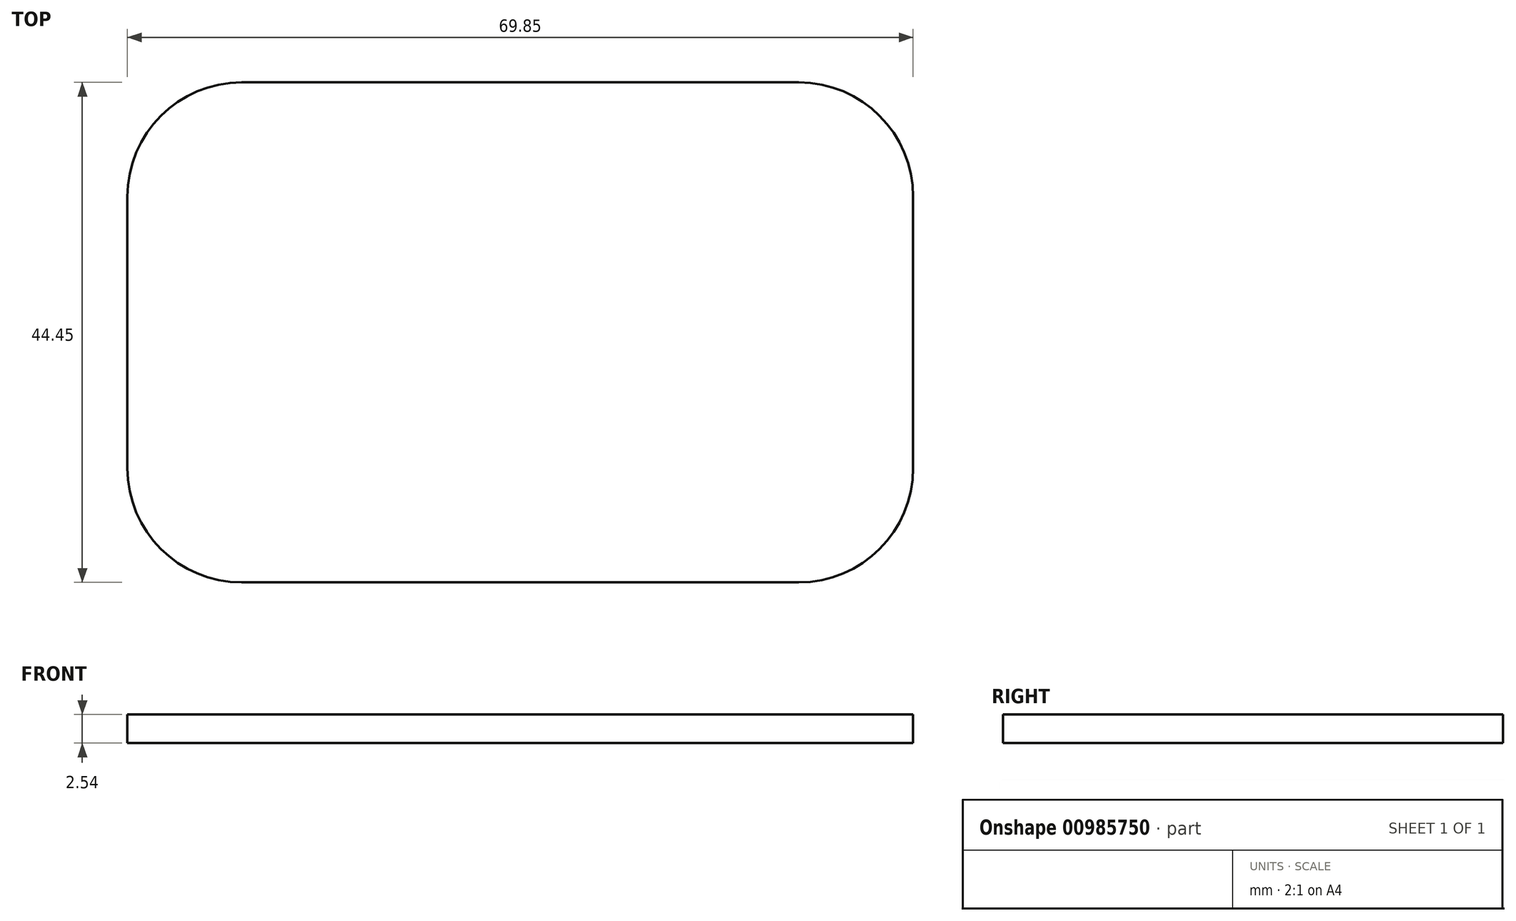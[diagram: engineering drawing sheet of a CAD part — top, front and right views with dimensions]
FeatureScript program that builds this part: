
annotation { "Feature Type Name" : "Feature", "Feature Type Description" : "" }
export const myFeature = defineFeature(function(context is Context, id is Id, definition is map)
    precondition{}
    {
        {
            var Q0;
            Q0=qCreatedBy(makeId("Top.planeOp"),FACE);
            var sketch = newSketch(context, id + "F0", { "sketchPlane" : qUnion([Q0])});
            skLineSegment(sketch, "E0.bottom", {"start": v(10.16, 0) * mm, "end": v(59.7, 0) * mm});
            skLineSegment(sketch, "E0.top", {"start": v(10.16, 44.45) * mm, "end": v(59.7, 44.45) * mm});
            skLineSegment(sketch, "E0.left", {"start": v(0, 10.16) * mm, "end": v(0, 34.3) * mm});
            skLineSegment(sketch, "E0.right", {"start": v(69.85, 10.16) * mm, "end": v(69.85, 34.3) * mm});
            skPoint(sketch, "E1.visualSharp", {"position": v(0, 44.45) * mm});
            skArc(sketch, "E1.filletArc", {"start": v(10.16, 44.45) * mm, "mid": v(2.98, 41.47) * mm, "end": v(0, 34.3) * mm});
            skPoint(sketch, "E2.visualSharp", {"position": v(69.85, 44.45) * mm});
            skArc(sketch, "E2.filletArc", {"start": v(69.85, 34.3) * mm, "mid": v(66.87, 41.47) * mm, "end": v(59.7, 44.45) * mm});
            skPoint(sketch, "E3.visualSharp", {"position": v(69.85, 0) * mm});
            skArc(sketch, "E3.filletArc", {"start": v(59.7, 0) * mm, "mid": v(66.87, 2.98) * mm, "end": v(69.85, 10.16) * mm});
            skPoint(sketch, "E4.visualSharp", {"position": v(0, 0) * mm});
            skArc(sketch, "E4.filletArc", {"start": v(0, 10.16) * mm, "mid": v(2.98, 2.98) * mm, "end": v(10.16, 0) * mm});
            skSolve(sketch);
        }
        {
            var Q0;
            Q0=makeQuery(id+"F0.imprint","IMPRINT",FACE,{"disambiguationData":[TD([[makeQuery(id+"F0.imprint","IMPRINT",EDGE,{"derivedFrom":sQuery(id+"F0.wireOp",EDGE,"E0.bottom")}),1.0]])]});
            extrude(context, id + "F1", {"entities" : qUnion([Q0]), "depth" : 2.54 * mm, "offsetDistance" : 25.4 * mm});
        }
    });
